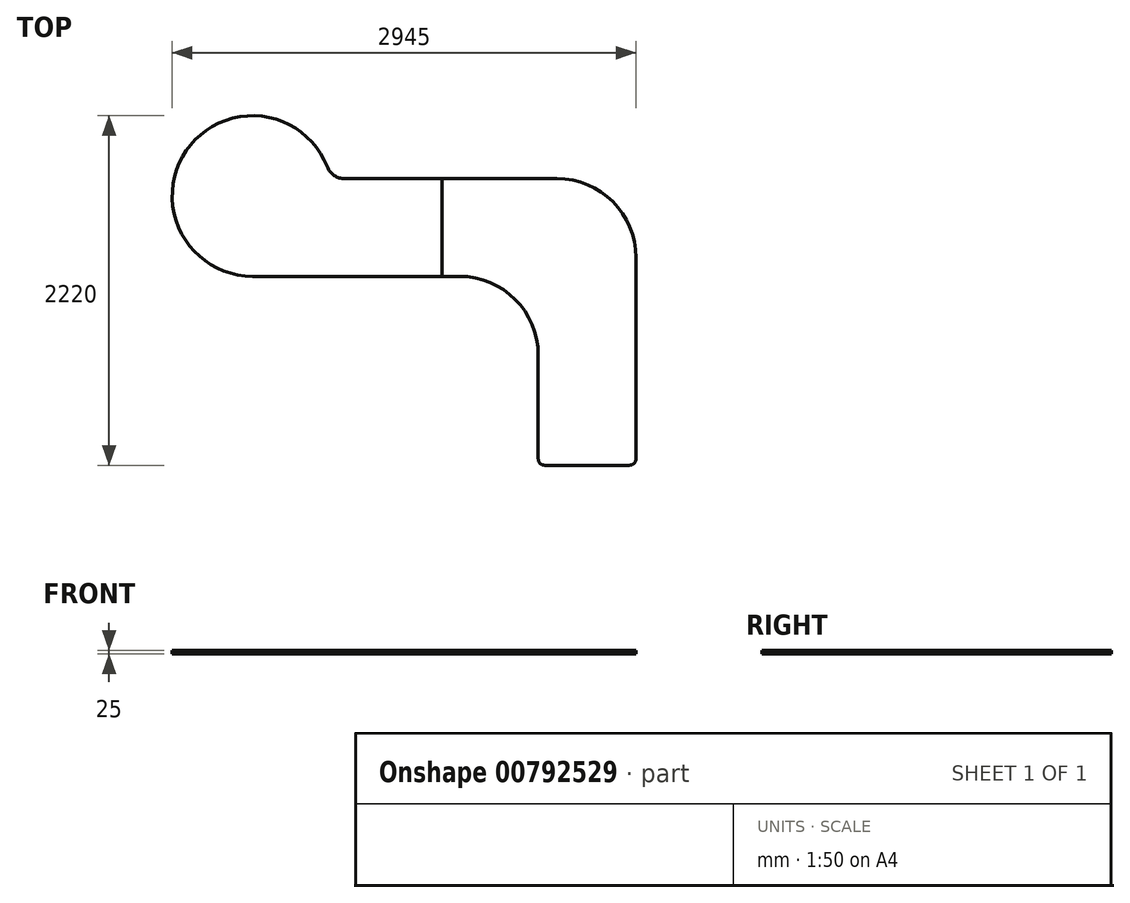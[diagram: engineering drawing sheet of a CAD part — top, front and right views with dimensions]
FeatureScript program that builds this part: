
annotation { "Feature Type Name" : "Feature", "Feature Type Description" : "" }
export const myFeature = defineFeature(function(context is Context, id is Id, definition is map)
    precondition{}
    {
        {
            var Q0;
            Q0=qCreatedBy(makeId("Top.planeOp"),FACE);
            var sketch = newSketch(context, id + "F0", { "sketchPlane" : qUnion([Q0])});
            skLineSegment(sketch, "E0", {"start": v(-88.07, -1116.76) * mm, "end": v(451.93, -1116.76) * mm});
            skLineSegment(sketch, "E1", {"start": v(491.93, -1076.76) * mm, "end": v(491.93, 203.24) * mm});
            skLineSegment(sketch, "E2", {"start": v(-8.07, 703.24) * mm, "end": v(-738.07, 703.24) * mm});
            skLineSegment(sketch, "E3", {"start": v(-738.07, 703.24) * mm, "end": v(-738.07, 83.24) * mm});
            skLineSegment(sketch, "E4", {"start": v(-738.07, 83.24) * mm, "end": v(-628.07, 83.24) * mm});
            skLineSegment(sketch, "E5", {"start": v(-128.07, -416.76) * mm, "end": v(-128.07, -1076.76) * mm});
            skPoint(sketch, "E6", {"position": v(-8.07, 703.24) * mm});
            skPoint(sketch, "E7", {"position": v(491.93, 203.24) * mm});
            skArc(sketch, "E8", {"start": v(491.93, 203.24) * mm, "mid": v(345.48, 556.79) * mm, "end": v(-8.07, 703.24) * mm});
            skPoint(sketch, "E9.orphan", {"position": v(491.93, 703.24) * mm});
            skPoint(sketch, "E10", {"position": v(-628.07, 83.24) * mm});
            skPoint(sketch, "E11", {"position": v(-128.07, -416.76) * mm});
            skArc(sketch, "E12", {"start": v(-128.07, -416.76) * mm, "mid": v(-274.52, -63.21) * mm, "end": v(-628.07, 83.24) * mm});
            skArc(sketch, "E13", {"start": v(-128.07, -1076.76) * mm, "mid": v(-116.36, -1105.05) * mm, "end": v(-88.07, -1116.76) * mm});
            skArc(sketch, "E14", {"start": v(451.93, -1116.76) * mm, "mid": v(480.21, -1105.05) * mm, "end": v(491.93, -1076.76) * mm});
            skSolve(sketch);
        }
        {
            var Q0;
            Q0=qCreatedBy(makeId("Top.planeOp"),FACE);
            var sketch = newSketch(context, id + "F1", { "sketchPlane" : qUnion([Q0])});
            skLineSegment(sketch, "E15", {"start": v(-738.07, 83.24) * mm, "end": v(-738.07, 703.24) * mm});
            skLineSegment(sketch, "E16", {"start": v(-738.07, 703.24) * mm, "end": v(-2441.07, 703.24) * mm});
            skLineSegment(sketch, "E17", {"start": v(-1943.07, 83.24) * mm, "end": v(-738.07, 83.24) * mm});
            skCircle(sketch, "E18", {"center": v(-1943.07, 593.24) * mm, "radius": 510 * mm});
            skPoint(sketch, "E19.end.orphan", {"position": v(-2453.07, 593.24) * mm});
            skArc(sketch, "E20", {"start": v(-1467.99, 778.7) * mm, "mid": v(-1424.41, 723.9) * mm, "end": v(-1357.53, 703.24) * mm});
            skSolve(sketch);
        }
        {
            var Q0;
            Q0=makeQuery(id+"F0.imprint","IMPRINT",FACE,{"disambiguationData":[TD([[makeQuery(id+"F0.imprint","IMPRINT",EDGE,{"derivedFrom":sQuery(id+"F0.wireOp",EDGE,"E0")}),1.0]])]});
            var Q1;
            {var subQ0=sQuery(id+"F1.wireOp",EDGE,"E18");var subQ1=sQuery(id+"F1.wireOp",EDGE,"E16");var subQ2=makeQuery(id+"F1.imprint","INTERSECT",VERTEX,{"disambiguationData":[OD(0.0)],"derivedFrom":[subQ1,subQ0]});Q1=makeQuery(id+"F1.imprint","IMPRINT",FACE,{"disambiguationData":[TD([[makeQuery(id+"F1.imprint","IMPRINT",EDGE,{"disambiguationData":[TD([[subQ2,1.0]])],"derivedFrom":subQ1}),1.0]])]});}
            var Q2;
            {var subQ0=sQuery(id+"F1.wireOp",EDGE,"E18");var subQ1=sQuery(id+"F1.wireOp",EDGE,"E16");var subQ2=makeQuery(id+"F1.imprint","INTERSECT",VERTEX,{"disambiguationData":[OD(0.0)],"derivedFrom":[subQ1,subQ0]});Q2=makeQuery(id+"F1.imprint","IMPRINT",FACE,{"disambiguationData":[TD([[makeQuery(id+"F1.imprint","IMPRINT",EDGE,{"disambiguationData":[TD([[subQ2,1.0]])],"derivedFrom":subQ1}),-1.0]])]});}
            var Q3;
            {var subQ0=sQuery(id+"F1.wireOp",EDGE,"E20");Q3=makeQuery(id+"F1.imprint","IMPRINT",FACE,{"disambiguationData":[TD([[makeQuery(id+"F1.imprint","IMPRINT",EDGE,{"derivedFrom":subQ0}),-1.0]])]});}
            var Q4;
            {var subQ5=sQuery(id+"F1.wireOp",EDGE,"E15");Q4=makeQuery(id+"F1.imprint","IMPRINT",FACE,{"disambiguationData":[TD([[makeQuery(id+"F1.imprint","IMPRINT",EDGE,{"derivedFrom":subQ5}),1.0]])]});}
            extrude(context, id + "F2", {"entities" : qUnion([Q0, Q1, Q2, Q3, Q4]), "depth" : 25 * mm, "offsetDistance" : 25 * mm});
        }
    });
